# Revit family: WH1140-36 GRAB BAR
name_source: partatom
category: Mechanical Equipment
revit_build: Autodesk Revit MEP 2016 (Build: 20150220_1215(x64)
units: mm (PartAtom-declared; Revit-internal decimal feet)

## family parameters
Cut with Voids When Loaded = No
Host = Face
OmniClass Number = 23.30.80.14
OmniClass Title = Handrails
Part Type = Normal
Room Calculation Point = No
Round Connector Dimension = Use Diameter
Shared = Yes

## types (1)
- WH1140-36
    Amperage = 0
    CW Connection = No
    Default Elevation = 34.313 "
    Description = WH1140-36 - Ligature Resistant Grab Bar With V Closure Strip 36 Inch Long
    HW Connection = No
    Manufacturer = Whitehall Mfg
    Material = Stainless Steel
    Model = WH1140-36
    OVERALL DEPTH = 1.5
    OVERALL SIZE HEIGHT = 3
    OVERALL SIZE WIDTH = 36
    Revised Date = 10/10/19
    Tempered Water Connection = No
    URL = https://www.whitehallmfg.com
    Vent Connection = No
    Voltage = 0
    Waste Connection = No

## geometry (parser evidence)
native form markers: Sweep x2
no freeform markers — native parametric forms only
